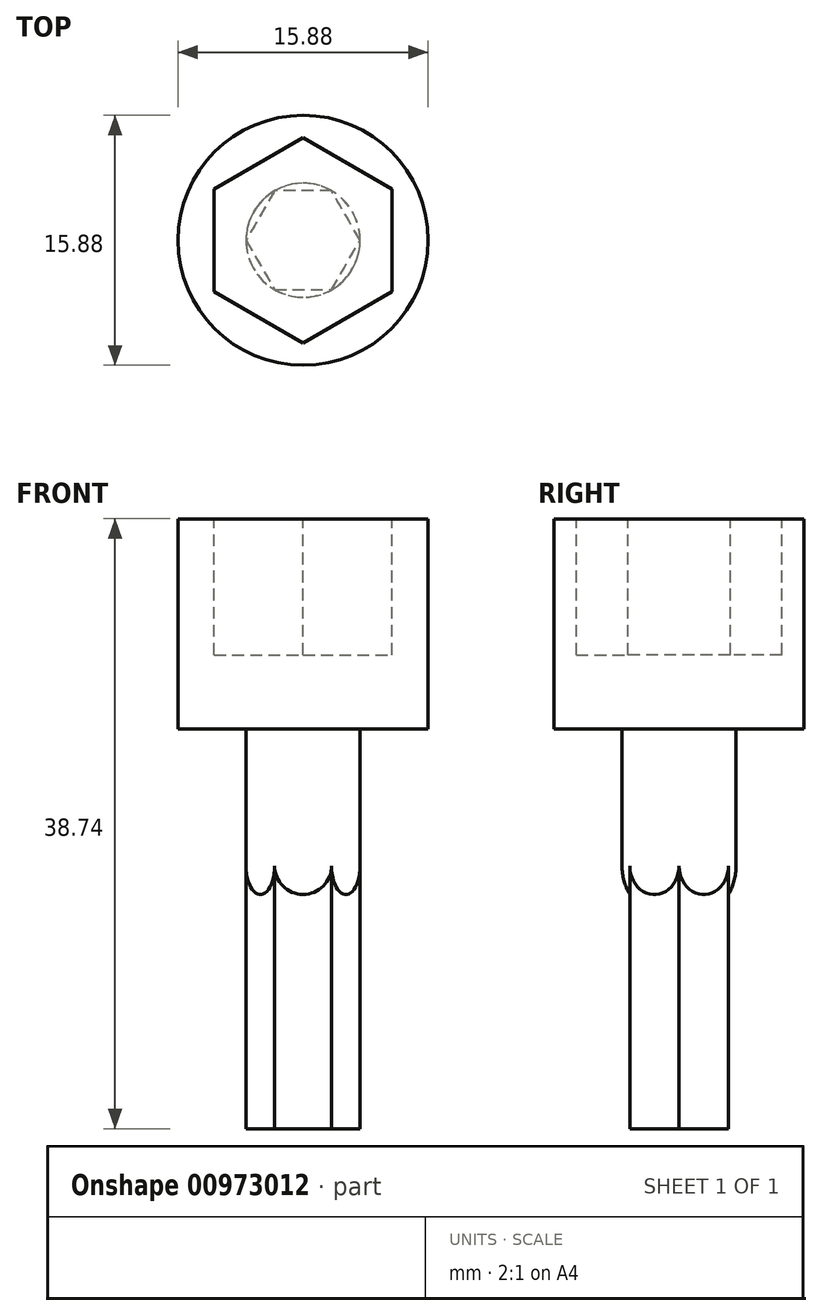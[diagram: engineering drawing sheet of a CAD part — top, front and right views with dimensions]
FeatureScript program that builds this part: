
annotation { "Feature Type Name" : "Feature", "Feature Type Description" : "" }
export const myFeature = defineFeature(function(context is Context, id is Id, definition is map)
    precondition{}
    {
        {
            var Q0;
            Q0=qCreatedBy(makeId("Top.planeOp"),FACE);
            var sketch = newSketch(context, id + "F0", { "sketchPlane" : qUnion([Q0])});
            skCircle(sketch, "E0", {"center": v(0, 0) * mm, "radius": 7.94 * mm});
            skSolve(sketch);
        }
        {
            var Q0;
            Q0=qSketchRegion(id+"F0",true);
            extrude(context, id + "F1", {"entities" : qUnion([Q0]), "depth" : 13.33 * mm, "offsetDistance" : 25.4 * mm});
        }
        {
            var Q0;
            Q0=makeQuery(id+"F1.opExtrude","CAP_FACE",FACE,{"disambiguationData":[OSD([sQuery(id+"F0.wireOp",EDGE,"E0")])],"isStart":false});
            var sketch = newSketch(context, id + "F2", { "sketchPlane" : qUnion([Q0])});
            skCircle(sketch, "E1.cCircle", {"center": v(0, 0) * mm, "radius": 5.65 * mm, "construction": true});
            skLineSegment(sketch, "E1.0", {"start": v(5.65, 3.26) * mm, "end": v(5.65, -3.26) * mm});
            skLineSegment(sketch, "E1.1", {"start": v(5.65, -3.26) * mm, "end": v(0, -6.53) * mm});
            skLineSegment(sketch, "E1.2", {"start": v(0, -6.53) * mm, "end": v(-5.65, -3.26) * mm});
            skLineSegment(sketch, "E1.3", {"start": v(-5.65, -3.26) * mm, "end": v(-5.65, 3.26) * mm});
            skLineSegment(sketch, "E1.4", {"start": v(-5.65, 3.26) * mm, "end": v(0, 6.53) * mm});
            skLineSegment(sketch, "E1.5", {"start": v(0, 6.53) * mm, "end": v(5.65, 3.26) * mm});
            skPoint(sketch, "E1.0.midPoint", {"position": v(5.65, 0) * mm});
            skSolve(sketch);
        }
        {
            var Q0;
            Q0=qSketchRegion(id+"F2",true);
            var Q1;
            Q1=makeQuery(id+"F2.imprint","IMPRINT",FACE,{"disambiguationData":[TD([[makeQuery(id+"F2.imprint","IMPRINT",EDGE,{"derivedFrom":sQuery(id+"F2.wireOp",EDGE,"E1.0")}),-1.0]])]});
            extrude(context, id + "F3", {"entities" : qUnion([Q0, Q1]), "operationType" : NewBodyOperationType.REMOVE, "oppositeDirection" : true, "depth" : 8.64 * mm, "offsetDistance" : 25.4 * mm});
        }
        {
            var Q0;
            Q0=makeQuery(id+"F1.opExtrude","CAP_FACE",FACE,{"disambiguationData":[OSD([sQuery(id+"F0.wireOp",EDGE,"E0")])],"isStart":true});
            var sketch = newSketch(context, id + "F4", { "sketchPlane" : qUnion([Q0])});
            skCircle(sketch, "E2.cCircle", {"center": v(0, 0) * mm, "radius": 3.14 * mm, "construction": true});
            skLineSegment(sketch, "E2.0", {"start": v(1.81, -3.14) * mm, "end": v(-1.81, -3.14) * mm});
            skLineSegment(sketch, "E2.1", {"start": v(-1.81, -3.14) * mm, "end": v(-3.62, 0) * mm});
            skLineSegment(sketch, "E2.2", {"start": v(-3.62, 0) * mm, "end": v(-1.81, 3.14) * mm});
            skLineSegment(sketch, "E2.3", {"start": v(-1.81, 3.14) * mm, "end": v(1.81, 3.14) * mm});
            skLineSegment(sketch, "E2.4", {"start": v(1.81, 3.14) * mm, "end": v(3.62, 0) * mm});
            skLineSegment(sketch, "E2.5", {"start": v(3.62, 0) * mm, "end": v(1.81, -3.14) * mm});
            skPoint(sketch, "E2.0.midPoint", {"position": v(0, -3.14) * mm});
            skSolve(sketch);
        }
        {
            var Q0;
            Q0=makeQuery(id+"F4.imprint","IMPRINT",FACE,{"disambiguationData":[TD([[makeQuery(id+"F4.imprint","IMPRINT",EDGE,{"derivedFrom":sQuery(id+"F4.wireOp",EDGE,"E2.0")}),-1.0]])]});
            extrude(context, id + "F5", {"entities" : qUnion([Q0]), "operationType" : NewBodyOperationType.ADD, "depth" : 25.4 * mm, "offsetDistance" : 25.4 * mm});
        }
        {
            var Q0;
            Q0=qCreatedBy(makeId("Front.planeOp"),FACE);
            var sketch = newSketch(context, id + "F6", { "sketchPlane" : qUnion([Q0])});
            skPoint(sketch, "E3.0", {"position": v(-3.62, 0) * mm});
            skPoint(sketch, "E3.1", {"position": v(3.62, 0) * mm});
            skLineSegment(sketch, "E4.bottom", {"start": v(-3.62, 0) * mm, "end": v(0, 0) * mm});
            skLineSegment(sketch, "E4.left", {"start": v(-3.62, 0) * mm, "end": v(-3.62, -8.71) * mm});
            skArc(sketch, "E5", {"start": v(-3.62, -8.71) * mm, "mid": v(-2.56, -11.27) * mm, "end": v(0, -12.33) * mm});
            skLineSegment(sketch, "E6", {"start": v(0, 0) * mm, "end": v(0, -12.33) * mm});
            skPoint(sketch, "E7.orphan", {"position": v(3.62, -8.71) * mm});
            skSolve(sketch);
        }
        {
            var Q0;
            Q0=qSketchRegion(id+"F6",true);
            var Q1;
            Q1=sQuery(id+"F6.wireOp",EDGE,"E6");
            revolve(context, id + "F7", {"operationType" : NewBodyOperationType.ADD, "surfaceOperationType" : NewSurfaceOperationType.NEW, "entities" : qUnion([Q0]), "axis" : qUnion([Q1]), "revolveType" : RevolveType.FULL});
        }
    });
